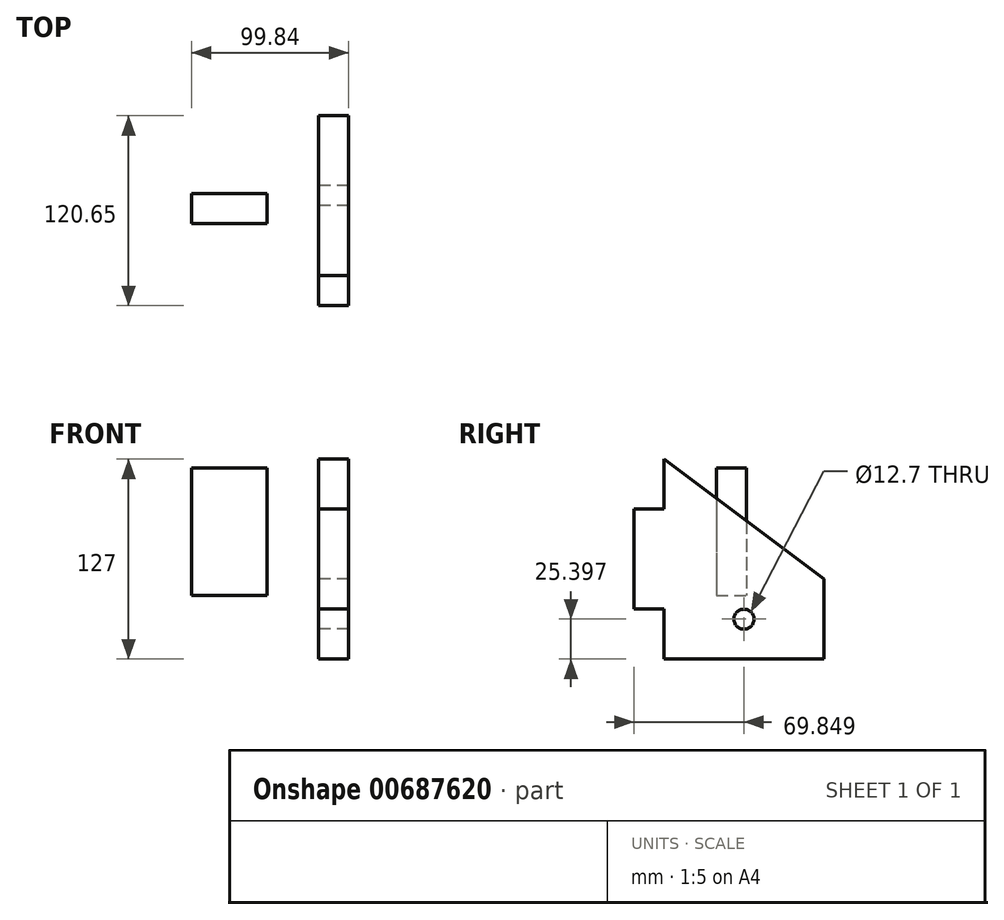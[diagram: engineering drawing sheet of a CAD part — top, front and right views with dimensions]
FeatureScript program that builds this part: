
annotation { "Feature Type Name" : "Feature", "Feature Type Description" : "" }
export const myFeature = defineFeature(function(context is Context, id is Id, definition is map)
    precondition{}
    {
        {
            var Q0;
            Q0=qCreatedBy(makeId("Right.planeOp"),FACE);
            var sketch = newSketch(context, id + "F0", { "sketchPlane" : qUnion([Q0])});
            skLineSegment(sketch, "E0", {"start": v(-52.25, 51.32) * mm, "end": v(-52.25, -75.68) * mm});
            skLineSegment(sketch, "E1", {"start": v(-52.25, -75.68) * mm, "end": v(49.35, -75.68) * mm});
            skLineSegment(sketch, "E2", {"start": v(49.35, -75.68) * mm, "end": v(49.35, -24.88) * mm});
            skLineSegment(sketch, "E3", {"start": v(49.35, -24.88) * mm, "end": v(-52.25, 51.32) * mm});
            skCircle(sketch, "E4", {"center": v(-1.45, -50.28) * mm, "radius": 6.35 * mm});
            skPoint(sketch, "E4.centerSnap0", {"position": v(49.35, -50.28) * mm});
            skPoint(sketch, "E4.centerSnap1", {"position": v(-1.45, -75.68) * mm});
            skPoint(sketch, "E5", {"position": v(-52.25, 19.57) * mm});
            skPoint(sketch, "E6", {"position": v(-52.25, -43.93) * mm});
            skLineSegment(sketch, "E7", {"start": v(-52.25, 19.57) * mm, "end": v(-71.3, 19.57) * mm});
            skLineSegment(sketch, "E8", {"start": v(-71.3, 19.57) * mm, "end": v(-71.3, -43.93) * mm});
            skLineSegment(sketch, "E9", {"start": v(-71.3, -43.93) * mm, "end": v(-52.25, -43.93) * mm});
            skSolve(sketch);
        }
        {
            var Q0;
            Q0 = qSketchRegion(id + "F0", true);
            extrude(context, id + "F1", {"entities" : qUnion([Q0]), "depth" : 19.05 * mm, "offsetDistance" : 25.4 * mm});
        }
        {
            var Q0;
            Q0=qCreatedBy(makeId("Front.planeOp"),FACE);
            var sketch = newSketch(context, id + "F2", { "sketchPlane" : qUnion([Q0])});
            skLineSegment(sketch, "E10.bottom", {"start": v(-80.79, 45.76) * mm, "end": v(-32.7, 45.76) * mm});
            skLineSegment(sketch, "E10.top", {"start": v(-80.79, -35.16) * mm, "end": v(-32.7, -35.16) * mm});
            skLineSegment(sketch, "E10.left", {"start": v(-80.79, 45.76) * mm, "end": v(-80.79, -35.16) * mm});
            skLineSegment(sketch, "E10.right", {"start": v(-32.7, 45.76) * mm, "end": v(-32.7, -35.16) * mm});
            skSolve(sketch);
        }
        {
            var Q0;
            Q0 = qSketchRegion(id + "F2", true);
            extrude(context, id + "F3", {"entities" : qUnion([Q0]), "depth" : 19.05 * mm, "offsetDistance" : 25.4 * mm});
        }
    });
